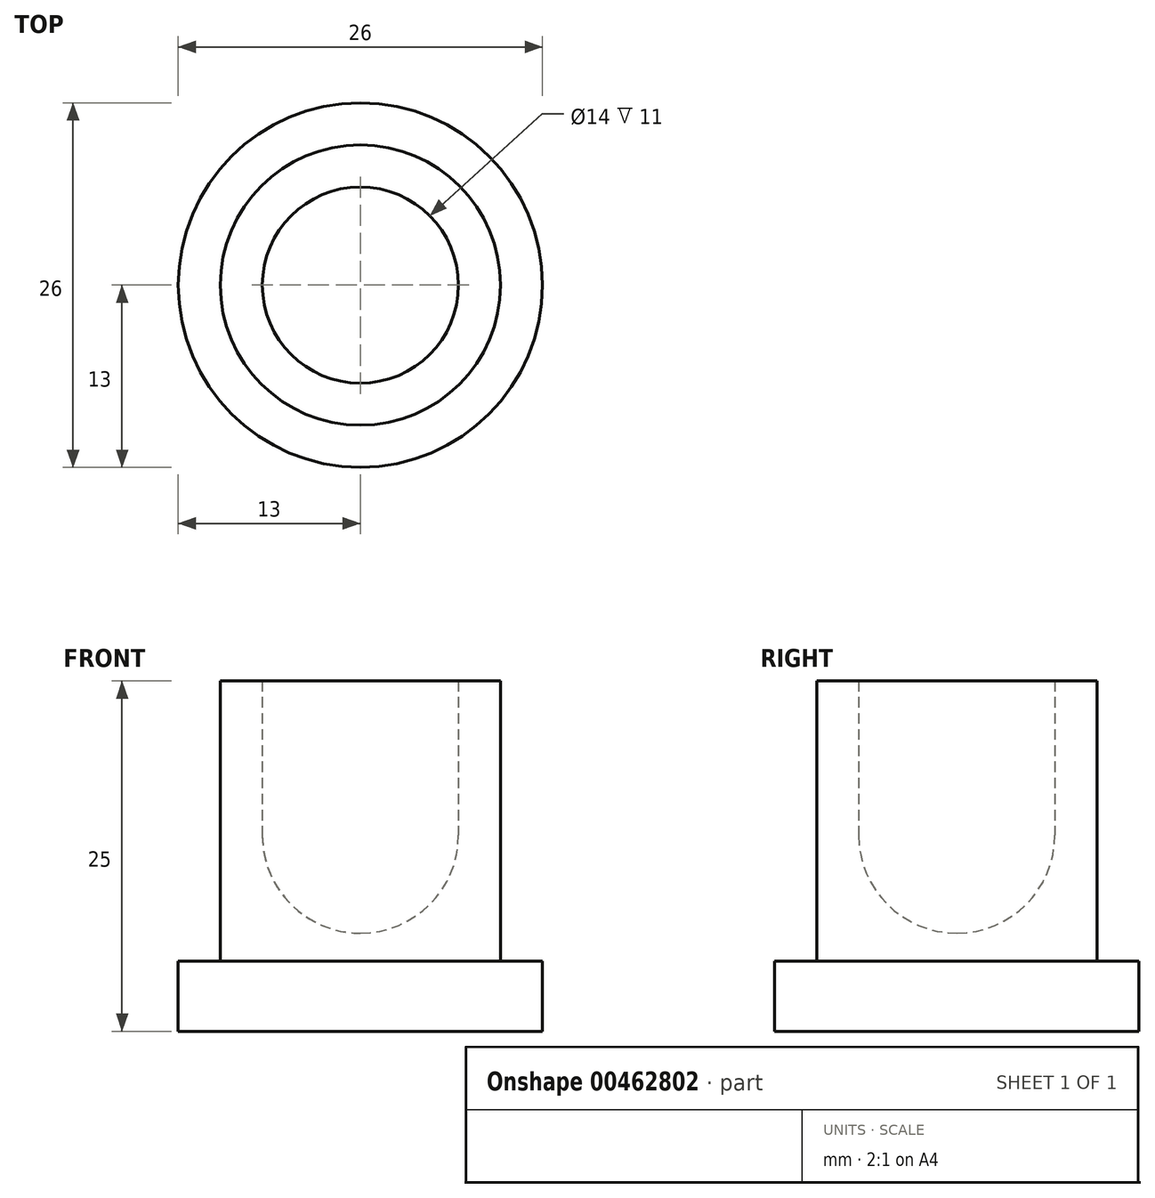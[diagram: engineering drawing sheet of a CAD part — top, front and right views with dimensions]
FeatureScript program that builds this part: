
annotation { "Feature Type Name" : "Feature", "Feature Type Description" : "" }
export const myFeature = defineFeature(function(context is Context, id is Id, definition is map)
    precondition{}
    {
        {
            var Q0;
            Q0=qCreatedBy(makeId("Top.planeOp"),FACE);
            var sketch = newSketch(context, id + "F0", { "sketchPlane" : qUnion([Q0])});
            skCircle(sketch, "E0", {"center": v(0, 0) * mm, "radius": 13 * mm});
            skCircle(sketch, "E1", {"center": v(0, 0) * mm, "radius": 10 * mm});
            skSolve(sketch);
        }
        {
            var Q0;
            Q0=makeQuery(id+"F0.imprint","IMPRINT",FACE,{"disambiguationData":[TD([[makeQuery(id+"F0.imprint","IMPRINT",EDGE,{"derivedFrom":sQuery(id+"F0.wireOp",EDGE,"E1")}),1.0]])]});
            var Q1;
            Q1=makeQuery(id+"F0.imprint","IMPRINT",FACE,{"disambiguationData":[TD([[makeQuery(id+"F0.imprint","IMPRINT",EDGE,{"derivedFrom":sQuery(id+"F0.wireOp",EDGE,"E0")}),1.0]])]});
            extrude(context, id + "F1", {"entities" : qUnion([Q0, Q1]), "depth" : 5 * mm});
        }
        {
            var Q0;
            Q0=makeQuery(id+"F0.imprint","IMPRINT",FACE,{"disambiguationData":[TD([[makeQuery(id+"F0.imprint","IMPRINT",EDGE,{"derivedFrom":sQuery(id+"F0.wireOp",EDGE,"E1")}),1.0]])]});
            extrude(context, id + "F2", {"entities" : qUnion([Q0]), "operationType" : NewBodyOperationType.ADD, "depth" : 25 * mm});
        }
        {
            var Q0;
            Q0=qCreatedBy(makeId("Front.planeOp"),FACE);
            var sketch = newSketch(context, id + "F3", { "sketchPlane" : qUnion([Q0])});
            skLineSegment(sketch, "E2", {"start": v(0, 25) * mm, "end": v(0, 7) * mm});
            skLineSegment(sketch, "E3", {"start": v(0, 25) * mm, "end": v(7, 25) * mm});
            skLineSegment(sketch, "E4", {"start": v(7, 25) * mm, "end": v(7, 14) * mm});
            skPoint(sketch, "E5", {"position": v(0, 14) * mm});
            skArc(sketch, "E6", {"start": v(0, 7) * mm, "mid": v(4.95, 9.05) * mm, "end": v(7, 14) * mm});
            skSolve(sketch);
        }
        {
            var Q0;
            Q0 = qSketchRegion(id + "F3", true);
            var Q1;
            Q1=sQuery(id+"F3.wireOp",EDGE,"E2");
            revolve(context, id + "F4", {"operationType" : NewBodyOperationType.REMOVE, "entities" : qUnion([Q0]), "axis" : qUnion([Q1]), "revolveType" : RevolveType.FULL, "oppositeDirection" : true});
        }
    });
